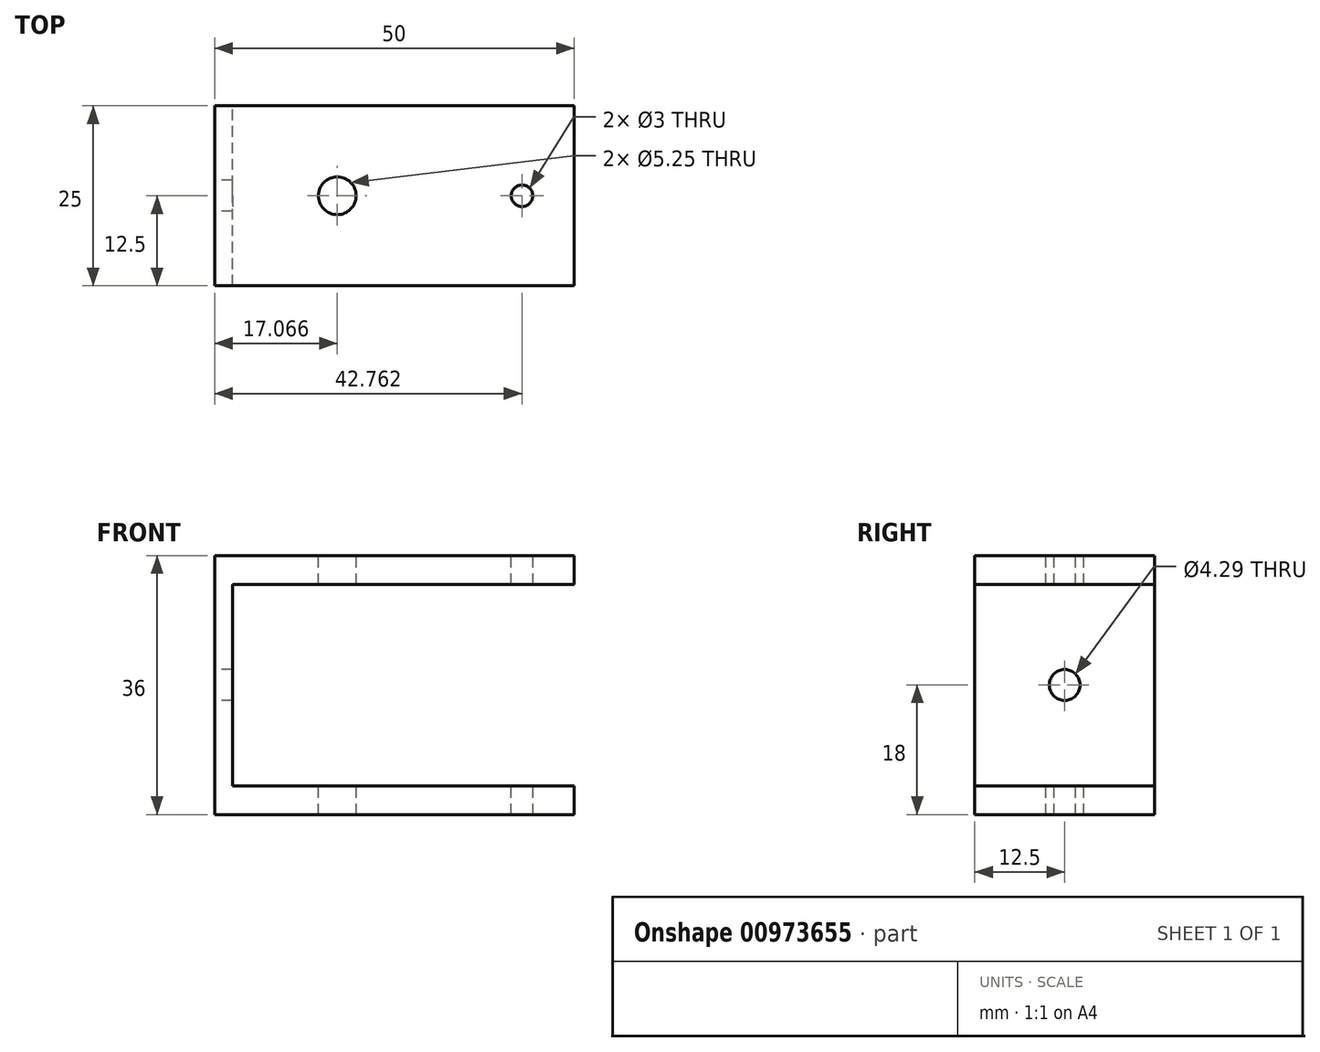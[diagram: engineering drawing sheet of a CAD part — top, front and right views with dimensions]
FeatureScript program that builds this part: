
annotation { "Feature Type Name" : "Feature", "Feature Type Description" : "" }
export const myFeature = defineFeature(function(context is Context, id is Id, definition is map)
    precondition{}
    {
        {
            var Q0;
            Q0=qCreatedBy(makeId("Front.planeOp"),FACE);
            var sketch = newSketch(context, id + "F0", { "sketchPlane" : qUnion([Q0])});
            skLineSegment(sketch, "E0.bottom", {"start": v(-25, 18) * mm, "end": v(25, 18) * mm});
            skLineSegment(sketch, "E0.top", {"start": v(-25, -18) * mm, "end": v(25, -18) * mm});
            skLineSegment(sketch, "E0.left", {"start": v(-25, 18) * mm, "end": v(-25, -18) * mm});
            skLineSegment(sketch, "E0.right", {"start": v(25, 18) * mm, "end": v(25, 14) * mm});
            skPoint(sketch, "E0.middle", {"position": v(0, 0) * mm});
            skLineSegment(sketch, "E1.bottom", {"start": v(-22.5, 14) * mm, "end": v(22.5, 14) * mm});
            skLineSegment(sketch, "E1.top", {"start": v(-22.5, -14) * mm, "end": v(22.5, -14) * mm});
            skLineSegment(sketch, "E1.left", {"start": v(-22.5, 14) * mm, "end": v(-22.5, -14) * mm});
            skLineSegment(sketch, "E2", {"start": v(22.5, 14) * mm, "end": v(25, 14) * mm});
            skLineSegment(sketch, "E3", {"start": v(25, -14) * mm, "end": v(22.5, -14) * mm});
            skLineSegment(sketch, "E4.trimOffspring", {"start": v(25, -14) * mm, "end": v(25, -18) * mm});
            skPoint(sketch, "E5.orphan", {"position": v(56.95, -14) * mm});
            skSolve(sketch);
        }
        {
            var Q0;
            Q0=makeQuery(id+"F0.imprint","IMPRINT",FACE,{"disambiguationData":[TD([[makeQuery(id+"F0.imprint","IMPRINT",EDGE,{"derivedFrom":sQuery(id+"F0.wireOp",EDGE,"E0.bottom")}),-1.0]])]});
            extrude(context, id + "F1", {"entities" : qUnion([Q0]), "depth" : 25 * mm, "offsetDistance" : 25 * mm});
        }
        {
            var Q0;
            Q0=makeQuery(id+"F1.opExtrude","SWEPT_FACE",FACE,{"disambiguationData":[OSD([sQuery(id+"F0.wireOp",EDGE,"E0.bottom")])]});
            var sketch = newSketch(context, id + "F2", { "sketchPlane" : qUnion([Q0])});
            skCircle(sketch, "E6", {"center": v(17.76, -12.5) * mm, "radius": 1.5 * mm});
            skPoint(sketch, "E6.centerSnap0", {"position": v(25, -12.5) * mm});
            skSolve(sketch);
        }
        {
            var Q0;
            Q0=makeQuery(id+"F2.imprint","IMPRINT",FACE,{"disambiguationData":[TD([[makeQuery(id+"F2.imprint","IMPRINT",EDGE,{"derivedFrom":sQuery(id+"F2.wireOp",EDGE,"E6")}),1.0]])]});
            extrude(context, id + "F3", {"entities" : qUnion([Q0]), "operationType" : NewBodyOperationType.REMOVE, "endBound" : BoundingType.THROUGH_ALL, "oppositeDirection" : true, "depth" : 25 * mm, "offsetDistance" : 25 * mm});
        }
        {
            var Q0;
            Q0=makeQuery(id+"F1.opExtrude","SWEPT_FACE",FACE,{"disambiguationData":[OSD([sQuery(id+"F0.wireOp",EDGE,"E0.left")])]});
            var sketch = newSketch(context, id + "F4", { "sketchPlane" : qUnion([Q0])});
            skCircle(sketch, "E7", {"center": v(12.5, 0) * mm, "radius": 2.15 * mm});
            skPoint(sketch, "E7.centerSnap0", {"position": v(12.5, 18) * mm});
            skPoint(sketch, "E7.centerSnap1", {"position": v(25, 0) * mm});
            skSolve(sketch);
        }
        {
            var Q0;
            Q0=makeQuery(id+"F4.imprint","IMPRINT",FACE,{"disambiguationData":[TD([[makeQuery(id+"F4.imprint","IMPRINT",EDGE,{"derivedFrom":sQuery(id+"F4.wireOp",EDGE,"E7")}),1.0]])]});
            extrude(context, id + "F5", {"entities" : qUnion([Q0]), "operationType" : NewBodyOperationType.REMOVE, "endBound" : BoundingType.THROUGH_ALL, "oppositeDirection" : true, "depth" : 25 * mm, "offsetDistance" : 25 * mm});
        }
        {
            var Q0;
            Q0=makeQuery(id+"F1.opExtrude","SWEPT_FACE",FACE,{"disambiguationData":[OSD([sQuery(id+"F0.wireOp",EDGE,"E0.bottom")])]});
            var sketch = newSketch(context, id + "F6", { "sketchPlane" : qUnion([Q0])});
            skCircle(sketch, "E8", {"center": v(-7.93, -12.5) * mm, "radius": 2.62 * mm});
            skPoint(sketch, "E8.centerSnap0", {"position": v(-25, -12.5) * mm});
            skSolve(sketch);
        }
        {
            var Q0;
            Q0=makeQuery(id+"F6.imprint","IMPRINT",FACE,{"disambiguationData":[TD([[makeQuery(id+"F6.imprint","IMPRINT",EDGE,{"derivedFrom":sQuery(id+"F6.wireOp",EDGE,"E8")}),1.0]])]});
            extrude(context, id + "F7", {"entities" : qUnion([Q0]), "operationType" : NewBodyOperationType.REMOVE, "endBound" : BoundingType.THROUGH_ALL, "oppositeDirection" : true, "depth" : 25 * mm, "offsetDistance" : 25 * mm});
        }
    });
